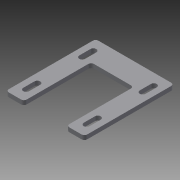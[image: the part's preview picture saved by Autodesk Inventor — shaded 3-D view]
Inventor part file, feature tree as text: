
AUTODESK INVENTOR PART (.ipt)
format: ipt  version: 2013 (Build 170138000, 138)  size: 117,760 bytes
history: native  units: in
note: dims shown in document units (in); Inventor stores cm internally (conversion verified against a paired STEP export)
features: extrude x1, fillet x1, mirror x1, sketch x1
ambient origin geometry x8: Origin, YZ Plane, XZ Plane, XY Plane, X Axis, Y Axis, Z Axis, Center Point
bodies: Solid1 (feature_tree)
feature tree (4):
  extrude  "Extrusion1"  Depth=0.1875in TaperAngle=0.0deg
  fillet  "Fillet1"  Radius=1.75in
  mirror  "Mirror2"
  sketch  "Sketch1"  dims[d1=4.0in d6=0.1875in d7=0.0in d8=1.75in d9=1.0in d11=0.26in d12=0.27in d13=0.27in d14=0.5in d15=0.5in d16=0.26in d17=0.5in d18=0.5in d19=0.8in d20=0.125in]
